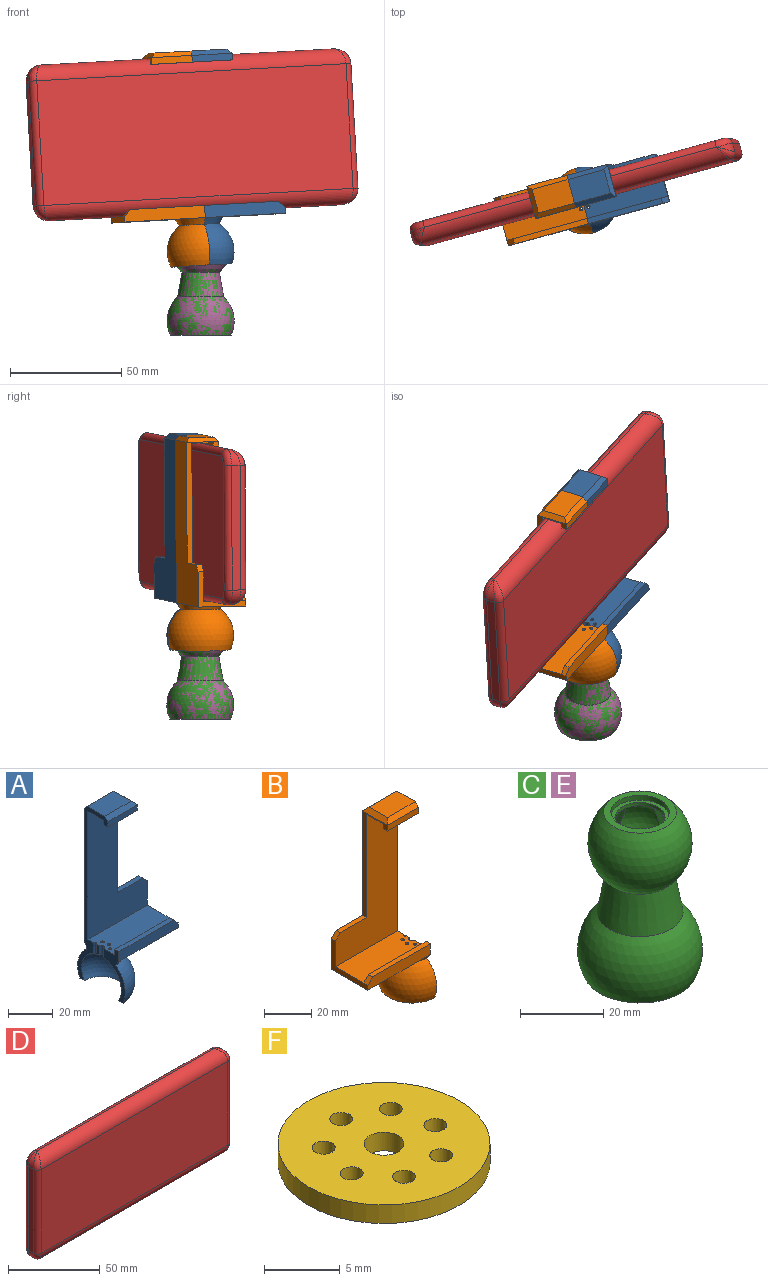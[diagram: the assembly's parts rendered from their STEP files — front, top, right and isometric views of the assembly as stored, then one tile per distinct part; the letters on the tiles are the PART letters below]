
ASSEMBLY  parts=6 mates=3
PART A: 32 faces, bbox 37.5x30x96.3 mm
  f0: plane 5.43x1.94mm, normal (-1,0,0), area 10.1mm2, adj f2,f6,f30,f31
  f1: plane 26.75x13.69mm, normal (-1,0,0), area 109.8mm2, adj f2,f4,f5,f6,f7,f8,f13,f15
  f2: plane 37.5x17mm, normal (0,0,1), area 628.6mm2, adj f0,f1,f3,f9,f15,f20,f27,f28
  f3: plane 96.25x19mm, normal (-1,0,0), area 298.5mm2, adj f2,f4,f5,f6,f7,f8,f12,f14
  f4: sphere r=15mm, area 860mm2, adj f1,f3,f5,f7
  f5: cone r=9mm half-angle=30deg, axis (0,0,1), area 107.4mm2, adj f1,f3,f4,f8
  f6: sphere r=12.5mm, area 727.1mm2, adj f0,f1,f3,f7,f27,f28,f29,f30
  f7: plane 27.27x13.64mm, normal (0,0,-1), area 108mm2, adj f1,f3,f4,f6
  f8: plane 37.5x22mm, normal (0,0,-1), area 644.1mm2, adj f1,f3,f5,f9,f13,f14
  f9: plane 22x15.75mm, normal (1,0,0), area 88.1mm2, adj f2,f8,f13,f14,f20,f22,f23
  f10: plane 15.75x2.5mm, normal (0,0,1), area 39.4mm2, adj f11,f14,f20,f22
  f11: plane 54.25x15mm, normal (1,0,0), area 148.1mm2, adj f10,f14,f16,f17,f18,f19,f20,f25
  f12: plane 16.75x11mm, normal (0,0,1), area 184.2mm2, adj f3,f24,f25,f26
  f13: plane 37.5x5.5mm, normal (0,-1,0), area 201.8mm2, adj f1,f8,f9,f21,f23
  f14: plane 73x37.5mm, normal (0,1,0), area 1715.8mm2, adj f3,f8,f9,f10,f11,f22,f26
  f15: plane 37.5x3mm, normal (0,1,0), area 108mm2, adj f1,f2,f21,f23
  f16: plane 18.75x3mm, normal (0,-1,0), area 56.3mm2, adj f3,f11,f17,f24
  f17: plane 18.75x2.5mm, normal (0,0,-1), area 46.9mm2, adj f3,f11,f16,f18
  f18: plane 18.75x2.5mm, normal (0,1,0), area 46.9mm2, adj f3,f11,f17,f19
  f19: plane 18.75x10mm, normal (0,0,-1), area 187.5mm2, adj f3,f11,f18,f20
  f20: plane 70x37.5mm, normal (0,-1,0), area 1612.7mm2, adj f2,f3,f9,f10,f11,f19,f22
  f21: plane 34.5x2.5mm, normal (0,0,1), area 86.2mm2, adj f1,f13,f15,f23
  f22: plane 3x3mm, normal (0.71,0,0.71), area 10.6mm2, adj f9,f10,f14,f20
  f23: plane 3x3mm, normal (0.71,0,0.71), area 10.6mm2, adj f9,f13,f15,f21
  f24: plane 18.75x2mm, normal (0,-0.71,0.71), area 50.2mm2, adj f3,f12,f16,f25
  f25: plane 15x2mm, normal (0.71,0,0.71), area 36.8mm2, adj f11,f12,f24,f26
  f26: plane 18.75x2mm, normal (0,0.71,0.71), area 50.2mm2, adj f3,f12,f14,f25
  f27: cylinder r=0.75mm len=5.94mm, axis (0,0,1), area 26.8mm2, adj f2,f6
  f28: cylinder r=0.75mm len=5.94mm, axis (0,0,1), area 26.8mm2, adj f2,f6
  f29: cylinder r=0.75mm len=5.94mm, axis (0,0,1), area 26.8mm2, adj f2,f6
  f30: cylinder r=1.31mm len=5.07mm, axis (0,0,1), area 20.9mm2, adj f0,f1,f2,f6
  f31: cylinder r=0.75mm len=5.94mm, axis (0,0,1), area 13.4mm2, adj f0,f2,f3,f6
PART B: 32 faces, bbox 37.5x30x96.3 mm
  f0: plane 5.43x1.94mm, normal (1,0,0), area 10.1mm2, adj f2,f6,f30,f31
  f1: plane 26.75x13.69mm, normal (1,0,0), area 109.8mm2, adj f2,f4,f5,f6,f7,f8,f13,f15
  f2: plane 37.5x17mm, normal (0,0,1), area 628.6mm2, adj f0,f1,f3,f9,f15,f20,f27,f28
  f3: plane 96.25x19mm, normal (1,0,0), area 298.5mm2, adj f2,f4,f5,f6,f7,f8,f12,f14
  f4: sphere r=15mm, area 860mm2, adj f1,f3,f5,f7
  f5: cone r=9mm half-angle=30deg, axis (0,0,1), area 107.4mm2, adj f1,f3,f4,f8
  f6: sphere r=12.5mm, area 727.1mm2, adj f0,f1,f3,f7,f27,f28,f29,f30
  f7: plane 27.27x13.64mm, normal (0,0,-1), area 108mm2, adj f1,f3,f4,f6
  f8: plane 37.5x22mm, normal (0,0,-1), area 644.1mm2, adj f1,f3,f5,f9,f13,f14
  f9: plane 22x15.75mm, normal (-1,0,0), area 88.1mm2, adj f2,f8,f13,f14,f20,f22,f23
  f10: plane 15.75x2.5mm, normal (0,0,1), area 39.4mm2, adj f11,f14,f20,f22
  f11: plane 54.25x15mm, normal (-1,0,0), area 148.1mm2, adj f10,f14,f16,f17,f18,f19,f20,f25
  f12: plane 16.75x11mm, normal (0,0,1), area 184.2mm2, adj f3,f24,f25,f26
  f13: plane 37.5x5.5mm, normal (0,-1,0), area 201.8mm2, adj f1,f8,f9,f21,f23
  f14: plane 73x37.5mm, normal (0,1,0), area 1715.8mm2, adj f3,f8,f9,f10,f11,f22,f26
  f15: plane 37.5x3mm, normal (0,1,0), area 108mm2, adj f1,f2,f21,f23
  f16: plane 18.75x3mm, normal (0,-1,0), area 56.3mm2, adj f3,f11,f17,f24
  f17: plane 18.75x2.5mm, normal (0,0,-1), area 46.9mm2, adj f3,f11,f16,f18
  f18: plane 18.75x2.5mm, normal (0,1,0), area 46.9mm2, adj f3,f11,f17,f19
  f19: plane 18.75x10mm, normal (0,0,-1), area 187.5mm2, adj f3,f11,f18,f20
  f20: plane 70x37.5mm, normal (0,-1,0), area 1612.7mm2, adj f2,f3,f9,f10,f11,f19,f22
  f21: plane 34.5x2.5mm, normal (0,0,1), area 86.2mm2, adj f1,f13,f15,f23
  f22: plane 3x3mm, normal (-0.71,0,0.71), area 10.6mm2, adj f9,f10,f14,f20
  f23: plane 3x3mm, normal (-0.71,0,0.71), area 10.6mm2, adj f9,f13,f15,f21
  f24: plane 18.75x2mm, normal (0,-0.71,0.71), area 50.2mm2, adj f3,f12,f16,f25
  f25: plane 15x2mm, normal (-0.71,0,0.71), area 36.8mm2, adj f11,f12,f24,f26
  f26: plane 18.75x2mm, normal (0,0.71,0.71), area 50.2mm2, adj f3,f12,f14,f25
  f27: cylinder r=0.75mm len=5.94mm, axis (0,0,1), area 26.8mm2, adj f2,f6
  f28: cylinder r=0.75mm len=5.94mm, axis (0,0,1), area 26.8mm2, adj f2,f6
  f29: cylinder r=0.75mm len=5.94mm, axis (0,0,1), area 26.8mm2, adj f2,f6
  f30: cylinder r=1.31mm len=5.07mm, axis (0,0,1), area 20.9mm2, adj f0,f1,f2,f6
  f31: cylinder r=0.75mm len=5.94mm, axis (0,0,1), area 13.4mm2, adj f0,f2,f3,f6
PART C: 28 faces, bbox 30x30x46.4 mm
  f0: plane 7.5x7.5mm, normal (0,0,-1), area 13.2mm2, adj f2,f8,f16,f17,f19,f20
  f1: plane 7.5x7.5mm, normal (0,0,-1), area 13.2mm2, adj f2,f8,f14,f15,f18,f20
  f2: sphere r=10mm, area 824.9mm2, adj f0,f1,f9,f14,f15,f16,f17,f18
  f3: cone r=10.31mm half-angle=10deg, axis (0,0,-1), area 659mm2, adj f4,f13
  f4: sphere r=12.5mm, area 1431.1mm2, adj f3,f5
  f5: plane 17.5x17.5mm, normal (0,0,1), area 86.5mm2, adj f4,f6
  f6: cylinder r=7mm len=14mm, axis (0,0,-1), area 62.8mm2, adj f5,f7
  f7: plane 14x14mm, normal (0,0,1), area 40.8mm2, adj f6,f8
  f8: cylinder r=6mm len=12mm, axis (0,0,-1), area 37.7mm2, adj f0,f1,f7,f21,f22
  f9: cone r=8mm half-angle=10deg, axis (0,0,-1), area 582.5mm2, adj f2,f10
  f10: sphere r=12.5mm, area 1029.2mm2, adj f9,f11
  f11: cylinder r=12mm len=24mm, axis (0,0,-1), area 207.3mm2, adj f10,f12
  f12: plane 27.27x27.27mm, normal (0,0,-1), area 131.8mm2, adj f11,f13
  f13: sphere r=15mm, area 1615.8mm2, adj f3,f12
  f14: plane 9.62x3.5mm, normal (0,0.94,-0.34), area 25.5mm2, adj f1,f2,f15,f22,f23
  f15: plane 9.5x3.92mm, normal (1,0,0), area 15.4mm2, adj f1,f2,f14
  f16: plane 9.62x3.5mm, normal (0,-0.94,-0.34), area 25.5mm2, adj f0,f2,f17,f21,f24
  f17: plane 9.5x3.92mm, normal (1,0,0), area 15.4mm2, adj f0,f2,f16
  f18: plane 9.5x3.92mm, normal (0,-1,0), area 15.4mm2, adj f1,f2,f20
  f19: plane 9.5x3.92mm, normal (0,1,0), area 15.4mm2, adj f0,f2,f20
  f20: plane 9.62x3.5mm, normal (-0.94,0,-0.34), area 25.5mm2, adj f0,f1,f2,f18,f19
  f21: plane 7.5x7.5mm, normal (0,0,-1), area 13.2mm2, adj f2,f8,f16,f24,f26,f27
  f22: plane 7.5x7.5mm, normal (0,0,-1), area 13.2mm2, adj f2,f8,f14,f23,f25,f27
  f23: plane 9.5x3.92mm, normal (-1,0,0), area 15.4mm2, adj f2,f14,f22
  f24: plane 9.5x3.92mm, normal (-1,0,0), area 15.4mm2, adj f2,f16,f21
  f25: plane 9.5x3.92mm, normal (0,-1,0), area 15.4mm2, adj f2,f22,f27
  f26: plane 9.5x3.92mm, normal (0,1,0), area 15.4mm2, adj f2,f21,f27
  f27: plane 9.62x3.5mm, normal (0.94,0,-0.34), area 25.5mm2, adj f2,f21,f22,f25,f26
PART D: 24 faces, bbox 151.2x10x71.2 mm
  f0: plane 56x4mm, normal (-1,0,0), area 224mm2, adj f1,f5,f14,f19
  f1: cylinder r=7mm len=7mm, axis (0,1,0), area 28mm2, adj f0,f15,f17
  f2: cylinder r=7mm len=7mm, axis (0,1,0), area 28mm2, adj f3,f12,f18
  f3: plane 56x4mm, normal (1,0,0), area 224mm2, adj f2,f4,f11,f20
  f4: cylinder r=7mm len=7mm, axis (0,1,0), area 28mm2, adj f3,f10,f22
  f5: cylinder r=7mm len=7mm, axis (0,1,0), area 28mm2, adj f0,f13,f21
  f6: plane 144x56mm, normal (0,-1,0), area 8064mm2, adj f8,f9,f11,f14
  f7: plane 144x64mm, normal (0,1,0), area 9202.3mm2, adj f16,f17,f18,f19,f20,f21,f22,f23
  f8: cylinder r=7mm len=144mm, axis (1,0,0), area 1551.4mm2, adj f6,f10,f13,f23
  f9: cylinder r=7mm len=144mm, axis (-1,0,0), area 1551.4mm2, adj f6,f12,f15,f16
  f10: bspline ~7.33x7mm, area 34.9mm2, adj f4,f8,f11
  f11: cylinder r=3mm len=56mm, axis (0,0,-1), area 263.9mm2, adj f3,f6,f10,f12
  f12: bspline ~8.3x7mm, area 34.9mm2, adj f2,f9,f11
  f13: bspline ~8.3x7mm, area 34.9mm2, adj f5,f8,f14
  f14: cylinder r=3mm len=56mm, axis (0,0,1), area 263.9mm2, adj f0,f6,f13,f15
  f15: bspline ~8.3x7mm, area 34.9mm2, adj f1,f9,f14
  f16: cylinder r=3mm len=136mm, axis (1,0,0), area 640.9mm2, adj f7,f9,f17,f18
  f17: torus R=4mm, axis (0,-1,0), area 43.7mm2, adj f1,f7,f16,f19
  f18: torus R=4mm, axis (0,-1,0), area 43.7mm2, adj f2,f7,f16,f20
  f19: cylinder r=3mm len=56mm, axis (0,0,-1), area 263.9mm2, adj f0,f7,f17,f21
  f20: cylinder r=3mm len=56mm, axis (0,0,1), area 263.9mm2, adj f3,f7,f18,f22
  f21: torus R=4mm, axis (0,-1,0), area 43.7mm2, adj f5,f7,f19,f23
  f22: torus R=4mm, axis (0,-1,0), area 43.7mm2, adj f4,f7,f20,f23
  f23: cylinder r=3mm len=136mm, axis (-1,0,0), area 640.9mm2, adj f7,f8,f21,f22
PART E: same geometry as C
PART F: 11 faces, bbox 14x14x1.5 mm
  f0: cylinder r=0.75mm len=1.5mm, axis (0,0,-1), area 7.1mm2, adj f9,f10
  f1: cylinder r=0.75mm len=1.5mm, axis (0,0,-1), area 7.1mm2, adj f9,f10
  f2: cylinder r=0.75mm len=1.5mm, axis (0,0,-1), area 7.1mm2, adj f9,f10
  f3: cylinder r=0.75mm len=1.5mm, axis (0,0,-1), area 7.1mm2, adj f9,f10
  f4: cylinder r=0.75mm len=1.5mm, axis (0,0,-1), area 7.1mm2, adj f9,f10
  f5: cylinder r=1.31mm len=2.63mm, axis (0,0,-1), area 12.4mm2, adj f9,f10
  f6: cylinder r=0.75mm len=1.5mm, axis (0,0,-1), area 7.1mm2, adj f9,f10
  f7: cylinder r=7mm len=14mm, axis (0,0,-1), area 66mm2, adj f9,f10
  f8: cylinder r=0.75mm len=1.5mm, axis (0,0,-1), area 7.1mm2, adj f9,f10
  f9: plane 14x14mm, normal (0,0,1), area 136.2mm2, adj f0,f1,f2,f3,f4,f5,f6,f7
  f10: plane 14x14mm, normal (0,0,-1), area 136.2mm2, adj f0,f1,f2,f3,f4,f5,f6,f7
PLACE A rot(axis=(-0.05,-0.2,0.98),15.7deg) t=(2.13,-0.23,0.06)mm
PLACE B rot(axis=(-0.05,-0.2,0.98),15.7deg) t=(2.13,-0.23,0.06)mm
PLACE C at identity
PLACE D rot(axis=(-0.05,-0.2,0.98),15.7deg) t=(-148.53,-32,26.27)mm
PLACE E rot(axis=(0,0,1),180deg) t=(0,0,0)mm
PLACE F at identity
MATE fastened D.f7 <-> A.f20  axis (-0.26,0.96,-0.02) through (-5.22,8.51,89.74)mm
MATE fastened F.f7 <-> C.f3  axis (0,0,-1) through (0,0,45)mm
MATE fastened B.f3 <-> A.f3  axis (0.96,0.26,0.05) through (-3.24,13.11,30.98)mm
